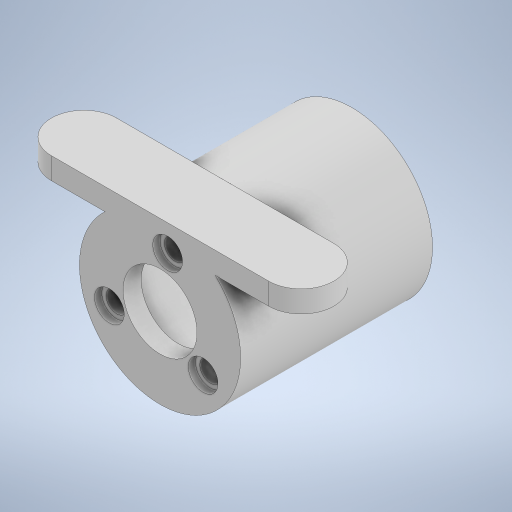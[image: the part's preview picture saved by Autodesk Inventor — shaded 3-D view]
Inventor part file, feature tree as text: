
AUTODESK INVENTOR PART (.ipt)
format: ipt  version: 2024.2 (Build 282272000, 272)  size: 290,816 bytes
history: native  units: mm
features: sketch x6, extrude x5, plane x1, hole x1
ambient origin geometry x8: Origin, YZ Plane, XZ Plane, XY Plane, X Axis, Y Axis, Z Axis, Center Point
bodies: Solid1 (feature_tree)
feature tree (13):
  extrude  "Extrusion1"  Depth=2.9mm
  extrude  "Extrusion2"  Depth=30.0mm TaperAngle=360.0deg
  extrude  "Extrusion3"  Depth=22.25mm
  plane  "Work Plane1"
  extrude  "Extrusion4"  Depth=1.5mm
  extrude  "Extrusion5"  Depth=1.0mm
  hole  "Hole1"  [1 undecoded]
  sketch  "Sketch1"  dims[d0=10.2mm d1=2.9mm]
  sketch  "Sketch2"  dims[d2=7.55mm d3=30.0mm d5=360.0deg]
  sketch  "Sketch3"  dims[d7=1.396263mm d8=22.25mm]
  sketch  "Sketch4"  dims[d9=1.5mm d10=0.0mm d11=4.1mm]
  sketch  "Sketch5"  dims[d12=1.0mm d13=0.0mm d14=20.25mm]
  sketch  "Sketch6"  dims[d15=24.0mm d16=0.0mm d17=11.125mm d18=9.0mm d19=30.0mm d20=15.0mm d21=3.0mm d22=0.0mm d23=1.5mm d24=0.0mm d25=2.9mm d26=6.0mm d27=4.1mm d28=1.0mm d29=90.0deg d30=8.0mm d31=20.594885mm]
note: 1 required parameter value undecoded (feature->parameter linkage not recoverable at this tier; creation-order binding heuristic only, values carry confidence <= 0.55)
